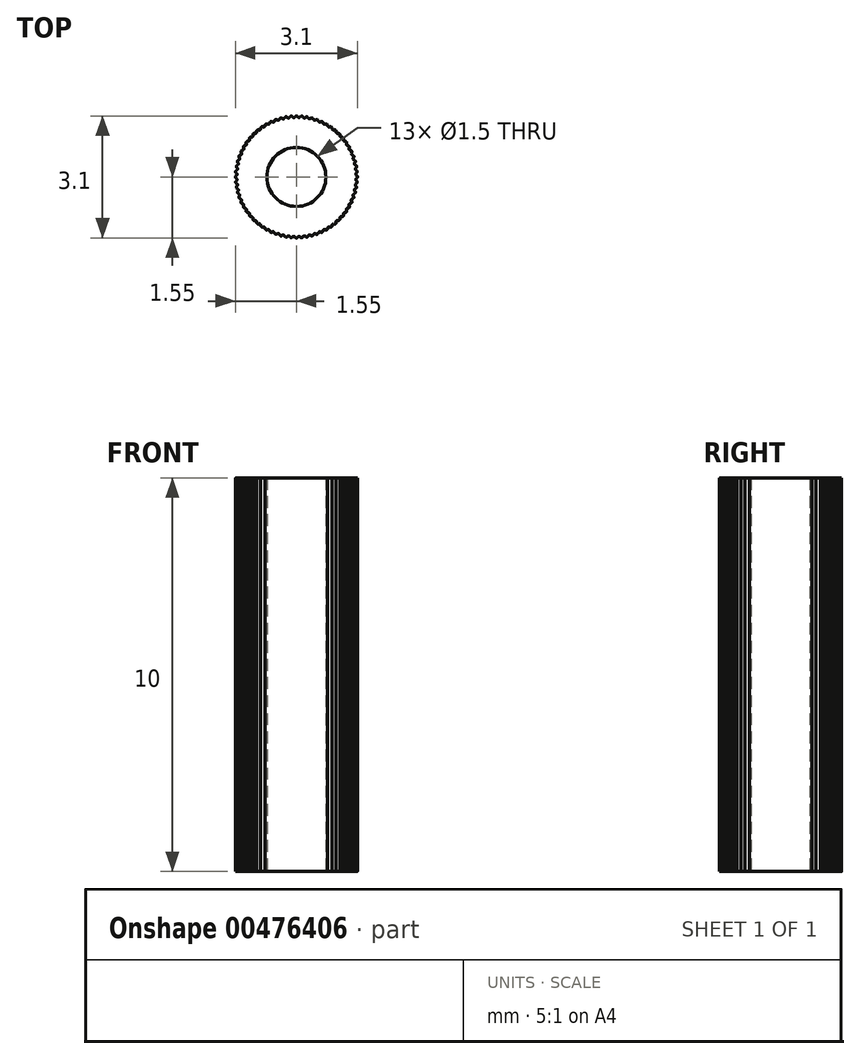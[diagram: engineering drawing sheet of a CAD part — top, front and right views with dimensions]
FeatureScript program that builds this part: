
annotation { "Feature Type Name" : "Feature", "Feature Type Description" : "" }
export const myFeature = defineFeature(function(context is Context, id is Id, definition is map)
    precondition{}
    {
        {
            var Q0;
            Q0=qCreatedBy(makeId("Top.planeOp"),FACE);
            var sketch = newSketch(context, id + "F0", { "sketchPlane" : qUnion([Q0])});
            skCircle(sketch, "E0", {"center": v(0, 0) * mm, "radius": 0.75 * mm});
            skCircle(sketch, "E1", {"center": v(0, 0) * mm, "radius": 1.55 * mm, "construction": true});
            skLineSegment(sketch, "E2", {"start": v(0, 0) * mm, "end": v(0, 1.55) * mm, "construction": true});
            skLineSegment(sketch, "E3", {"start": v(0, 0) * mm, "end": v(0.14, 1.54) * mm, "construction": true});
            skArc(sketch, "E4", {"start": v(0.03, 1.53) * mm, "mid": v(0.02, 1.54) * mm, "end": v(0, 1.55) * mm});
            skArc(sketch, "E5", {"start": v(0.03, 1.53) * mm, "mid": v(0.07, 1.51) * mm, "end": v(0.1, 1.53) * mm});
            skArc(sketch, "E6", {"start": v(0.14, 1.54) * mm, "mid": v(0.12, 1.54) * mm, "end": v(0.1, 1.53) * mm});
            skCircle(sketch, "E7", {"center": v(0, 0) * mm, "radius": 1.51 * mm, "construction": true});
            skArc(sketch, "E8.1.0", {"start": v(-0.1, 1.53) * mm, "mid": v(-0.12, 1.54) * mm, "end": v(-0.14, 1.54) * mm});
            skArc(sketch, "E8.1.1", {"start": v(-0.1, 1.53) * mm, "mid": v(-0.07, 1.51) * mm, "end": v(-0.03, 1.53) * mm});
            skArc(sketch, "E8.1.2", {"start": v(0, 1.55) * mm, "mid": v(-0.02, 1.54) * mm, "end": v(-0.03, 1.53) * mm});
            skArc(sketch, "E8.2.0", {"start": v(-0.23, 1.51) * mm, "mid": v(-0.25, 1.52) * mm, "end": v(-0.27, 1.53) * mm});
            skArc(sketch, "E8.2.1", {"start": v(-0.23, 1.51) * mm, "mid": v(-0.2, 1.5) * mm, "end": v(-0.17, 1.52) * mm});
            skArc(sketch, "E8.2.2", {"start": v(-0.14, 1.54) * mm, "mid": v(-0.15, 1.54) * mm, "end": v(-0.17, 1.52) * mm});
            skArc(sketch, "E8.3.0", {"start": v(-0.36, 1.49) * mm, "mid": v(-0.38, 1.5) * mm, "end": v(-0.4, 1.5) * mm});
            skArc(sketch, "E8.3.1", {"start": v(-0.36, 1.49) * mm, "mid": v(-0.33, 1.48) * mm, "end": v(-0.3, 1.5) * mm});
            skArc(sketch, "E8.3.2", {"start": v(-0.27, 1.53) * mm, "mid": v(-0.29, 1.52) * mm, "end": v(-0.3, 1.5) * mm});
            skArc(sketch, "E8.4.0", {"start": v(-0.5, 1.45) * mm, "mid": v(-0.5, 1.46) * mm, "end": v(-0.53, 1.46) * mm});
            skArc(sketch, "E8.4.1", {"start": v(-0.5, 1.45) * mm, "mid": v(-0.45, 1.44) * mm, "end": v(-0.43, 1.47) * mm});
            skArc(sketch, "E8.4.2", {"start": v(-0.4, 1.5) * mm, "mid": v(-0.42, 1.49) * mm, "end": v(-0.43, 1.47) * mm});
            skArc(sketch, "E8.5.0", {"start": v(-0.62, 1.4) * mm, "mid": v(-0.63, 1.4) * mm, "end": v(-0.66, 1.4) * mm});
            skArc(sketch, "E8.5.1", {"start": v(-0.62, 1.4) * mm, "mid": v(-0.58, 1.4) * mm, "end": v(-0.56, 1.43) * mm});
            skArc(sketch, "E8.5.2", {"start": v(-0.53, 1.46) * mm, "mid": v(-0.55, 1.44) * mm, "end": v(-0.56, 1.43) * mm});
            skArc(sketch, "E8.6.0", {"start": v(-0.74, 1.34) * mm, "mid": v(-0.76, 1.35) * mm, "end": v(-0.78, 1.34) * mm});
            skArc(sketch, "E8.6.1", {"start": v(-0.74, 1.34) * mm, "mid": v(-0.7, 1.34) * mm, "end": v(-0.68, 1.37) * mm});
            skArc(sketch, "E8.6.2", {"start": v(-0.66, 1.4) * mm, "mid": v(-0.67, 1.4) * mm, "end": v(-0.68, 1.37) * mm});
            skArc(sketch, "E8.7.0", {"start": v(-0.85, 1.27) * mm, "mid": v(-0.87, 1.28) * mm, "end": v(-0.89, 1.27) * mm});
            skArc(sketch, "E8.7.1", {"start": v(-0.85, 1.27) * mm, "mid": v(-0.81, 1.27) * mm, "end": v(-0.8, 1.3) * mm});
            skArc(sketch, "E8.7.2", {"start": v(-0.78, 1.34) * mm, "mid": v(-0.79, 1.33) * mm, "end": v(-0.8, 1.3) * mm});
            skArc(sketch, "E8.8.0", {"start": v(-0.96, 1.2) * mm, "mid": v(-0.98, 1.2) * mm, "end": v(-1, 1.19) * mm});
            skArc(sketch, "E8.8.1", {"start": v(-0.96, 1.2) * mm, "mid": v(-0.92, 1.2) * mm, "end": v(-0.9, 1.23) * mm});
            skArc(sketch, "E8.8.2", {"start": v(-0.89, 1.27) * mm, "mid": v(-0.9, 1.25) * mm, "end": v(-0.9, 1.23) * mm});
            skArc(sketch, "E8.9.0", {"start": v(-1.06, 1.1) * mm, "mid": v(-1.08, 1.1) * mm, "end": v(-1.1, 1.1) * mm});
            skArc(sketch, "E8.9.1", {"start": v(-1.06, 1.1) * mm, "mid": v(-1.02, 1.11) * mm, "end": v(-1, 1.15) * mm});
            skArc(sketch, "E8.9.2", {"start": v(-1, 1.19) * mm, "mid": v(-1, 1.17) * mm, "end": v(-1, 1.15) * mm});
            skArc(sketch, "E8.10.0", {"start": v(-1.15, 1) * mm, "mid": v(-1.17, 1) * mm, "end": v(-1.19, 1) * mm});
            skArc(sketch, "E8.10.1", {"start": v(-1.15, 1) * mm, "mid": v(-1.11, 1.02) * mm, "end": v(-1.1, 1.06) * mm});
            skArc(sketch, "E8.10.2", {"start": v(-1.1, 1.1) * mm, "mid": v(-1.1, 1.08) * mm, "end": v(-1.1, 1.06) * mm});
            skArc(sketch, "E8.11.0", {"start": v(-1.23, 0.9) * mm, "mid": v(-1.25, 0.9) * mm, "end": v(-1.27, 0.89) * mm});
            skArc(sketch, "E8.11.1", {"start": v(-1.23, 0.9) * mm, "mid": v(-1.2, 0.92) * mm, "end": v(-1.2, 0.96) * mm});
            skArc(sketch, "E8.11.2", {"start": v(-1.19, 1) * mm, "mid": v(-1.2, 0.98) * mm, "end": v(-1.2, 0.96) * mm});
            skArc(sketch, "E8.12.0", {"start": v(-1.3, 0.8) * mm, "mid": v(-1.33, 0.79) * mm, "end": v(-1.34, 0.78) * mm});
            skArc(sketch, "E8.12.1", {"start": v(-1.3, 0.8) * mm, "mid": v(-1.27, 0.81) * mm, "end": v(-1.27, 0.85) * mm});
            skArc(sketch, "E8.12.2", {"start": v(-1.27, 0.89) * mm, "mid": v(-1.28, 0.87) * mm, "end": v(-1.27, 0.85) * mm});
            skArc(sketch, "E8.13.0", {"start": v(-1.37, 0.68) * mm, "mid": v(-1.4, 0.67) * mm, "end": v(-1.4, 0.66) * mm});
            skArc(sketch, "E8.13.1", {"start": v(-1.37, 0.68) * mm, "mid": v(-1.34, 0.7) * mm, "end": v(-1.34, 0.74) * mm});
            skArc(sketch, "E8.13.2", {"start": v(-1.34, 0.77) * mm, "mid": v(-1.35, 0.76) * mm, "end": v(-1.34, 0.74) * mm});
            skArc(sketch, "E8.14.0", {"start": v(-1.43, 0.56) * mm, "mid": v(-1.44, 0.55) * mm, "end": v(-1.46, 0.53) * mm});
            skArc(sketch, "E8.14.1", {"start": v(-1.43, 0.56) * mm, "mid": v(-1.4, 0.58) * mm, "end": v(-1.4, 0.62) * mm});
            skArc(sketch, "E8.14.2", {"start": v(-1.4, 0.66) * mm, "mid": v(-1.4, 0.63) * mm, "end": v(-1.4, 0.62) * mm});
            skArc(sketch, "E8.15.0", {"start": v(-1.47, 0.43) * mm, "mid": v(-1.49, 0.42) * mm, "end": v(-1.5, 0.4) * mm});
            skArc(sketch, "E8.15.1", {"start": v(-1.47, 0.43) * mm, "mid": v(-1.44, 0.45) * mm, "end": v(-1.45, 0.5) * mm});
            skArc(sketch, "E8.15.2", {"start": v(-1.46, 0.53) * mm, "mid": v(-1.46, 0.5) * mm, "end": v(-1.45, 0.5) * mm});
            skArc(sketch, "E8.16.0", {"start": v(-1.5, 0.3) * mm, "mid": v(-1.52, 0.29) * mm, "end": v(-1.53, 0.27) * mm});
            skArc(sketch, "E8.16.1", {"start": v(-1.5, 0.3) * mm, "mid": v(-1.48, 0.33) * mm, "end": v(-1.49, 0.36) * mm});
            skArc(sketch, "E8.16.2", {"start": v(-1.5, 0.4) * mm, "mid": v(-1.5, 0.38) * mm, "end": v(-1.49, 0.36) * mm});
            skArc(sketch, "E8.17.0", {"start": v(-1.52, 0.17) * mm, "mid": v(-1.54, 0.15) * mm, "end": v(-1.54, 0.14) * mm});
            skArc(sketch, "E8.17.1", {"start": v(-1.52, 0.17) * mm, "mid": v(-1.5, 0.2) * mm, "end": v(-1.51, 0.23) * mm});
            skArc(sketch, "E8.17.2", {"start": v(-1.53, 0.27) * mm, "mid": v(-1.52, 0.25) * mm, "end": v(-1.51, 0.23) * mm});
            skArc(sketch, "E8.18.0", {"start": v(-1.53, 0.03) * mm, "mid": v(-1.54, 0.02) * mm, "end": v(-1.55, 0) * mm});
            skArc(sketch, "E8.18.1", {"start": v(-1.53, 0.03) * mm, "mid": v(-1.51, 0.07) * mm, "end": v(-1.53, 0.1) * mm});
            skArc(sketch, "E8.18.2", {"start": v(-1.54, 0.14) * mm, "mid": v(-1.54, 0.12) * mm, "end": v(-1.53, 0.1) * mm});
            skArc(sketch, "E8.19.0", {"start": v(-1.53, -0.1) * mm, "mid": v(-1.54, -0.12) * mm, "end": v(-1.54, -0.14) * mm});
            skArc(sketch, "E8.19.1", {"start": v(-1.53, -0.1) * mm, "mid": v(-1.51, -0.07) * mm, "end": v(-1.53, -0.03) * mm});
            skArc(sketch, "E8.19.2", {"start": v(-1.55, 0) * mm, "mid": v(-1.54, -0.02) * mm, "end": v(-1.53, -0.03) * mm});
            skArc(sketch, "E8.20.0", {"start": v(-1.51, -0.23) * mm, "mid": v(-1.52, -0.25) * mm, "end": v(-1.53, -0.27) * mm});
            skArc(sketch, "E8.20.1", {"start": v(-1.51, -0.23) * mm, "mid": v(-1.5, -0.2) * mm, "end": v(-1.52, -0.17) * mm});
            skArc(sketch, "E8.20.2", {"start": v(-1.54, -0.14) * mm, "mid": v(-1.54, -0.15) * mm, "end": v(-1.52, -0.17) * mm});
            skArc(sketch, "E8.21.0", {"start": v(-1.49, -0.36) * mm, "mid": v(-1.5, -0.38) * mm, "end": v(-1.5, -0.4) * mm});
            skArc(sketch, "E8.21.1", {"start": v(-1.49, -0.36) * mm, "mid": v(-1.48, -0.33) * mm, "end": v(-1.5, -0.3) * mm});
            skArc(sketch, "E8.21.2", {"start": v(-1.53, -0.27) * mm, "mid": v(-1.52, -0.29) * mm, "end": v(-1.5, -0.3) * mm});
            skArc(sketch, "E8.22.0", {"start": v(-1.45, -0.5) * mm, "mid": v(-1.46, -0.5) * mm, "end": v(-1.46, -0.53) * mm});
            skArc(sketch, "E8.22.1", {"start": v(-1.45, -0.5) * mm, "mid": v(-1.44, -0.45) * mm, "end": v(-1.47, -0.43) * mm});
            skArc(sketch, "E8.22.2", {"start": v(-1.5, -0.4) * mm, "mid": v(-1.49, -0.42) * mm, "end": v(-1.47, -0.43) * mm});
            skArc(sketch, "E8.23.0", {"start": v(-1.4, -0.62) * mm, "mid": v(-1.4, -0.63) * mm, "end": v(-1.4, -0.66) * mm});
            skArc(sketch, "E8.23.1", {"start": v(-1.4, -0.62) * mm, "mid": v(-1.4, -0.58) * mm, "end": v(-1.43, -0.56) * mm});
            skArc(sketch, "E8.23.2", {"start": v(-1.46, -0.53) * mm, "mid": v(-1.44, -0.55) * mm, "end": v(-1.43, -0.56) * mm});
            skArc(sketch, "E8.24.0", {"start": v(-1.34, -0.74) * mm, "mid": v(-1.35, -0.76) * mm, "end": v(-1.34, -0.77) * mm});
            skArc(sketch, "E8.24.1", {"start": v(-1.34, -0.74) * mm, "mid": v(-1.34, -0.7) * mm, "end": v(-1.37, -0.68) * mm});
            skArc(sketch, "E8.24.2", {"start": v(-1.4, -0.66) * mm, "mid": v(-1.4, -0.67) * mm, "end": v(-1.37, -0.68) * mm});
            skArc(sketch, "E8.25.0", {"start": v(-1.27, -0.85) * mm, "mid": v(-1.28, -0.87) * mm, "end": v(-1.27, -0.89) * mm});
            skArc(sketch, "E8.25.1", {"start": v(-1.27, -0.85) * mm, "mid": v(-1.27, -0.81) * mm, "end": v(-1.3, -0.8) * mm});
            skArc(sketch, "E8.25.2", {"start": v(-1.34, -0.78) * mm, "mid": v(-1.33, -0.79) * mm, "end": v(-1.3, -0.8) * mm});
            skArc(sketch, "E8.26.0", {"start": v(-1.2, -0.96) * mm, "mid": v(-1.2, -0.98) * mm, "end": v(-1.19, -1) * mm});
            skArc(sketch, "E8.26.1", {"start": v(-1.2, -0.96) * mm, "mid": v(-1.2, -0.92) * mm, "end": v(-1.23, -0.9) * mm});
            skArc(sketch, "E8.26.2", {"start": v(-1.27, -0.89) * mm, "mid": v(-1.25, -0.9) * mm, "end": v(-1.23, -0.9) * mm});
            skArc(sketch, "E8.27.0", {"start": v(-1.1, -1.06) * mm, "mid": v(-1.1, -1.08) * mm, "end": v(-1.1, -1.1) * mm});
            skArc(sketch, "E8.27.1", {"start": v(-1.1, -1.06) * mm, "mid": v(-1.11, -1.02) * mm, "end": v(-1.15, -1) * mm});
            skArc(sketch, "E8.27.2", {"start": v(-1.19, -1) * mm, "mid": v(-1.17, -1) * mm, "end": v(-1.15, -1) * mm});
            skArc(sketch, "E8.28.0", {"start": v(-1, -1.15) * mm, "mid": v(-1, -1.17) * mm, "end": v(-1, -1.19) * mm});
            skArc(sketch, "E8.28.1", {"start": v(-1, -1.15) * mm, "mid": v(-1.02, -1.11) * mm, "end": v(-1.06, -1.1) * mm});
            skArc(sketch, "E8.28.2", {"start": v(-1.1, -1.1) * mm, "mid": v(-1.08, -1.1) * mm, "end": v(-1.06, -1.1) * mm});
            skArc(sketch, "E8.29.0", {"start": v(-0.9, -1.23) * mm, "mid": v(-0.9, -1.25) * mm, "end": v(-0.89, -1.27) * mm});
            skArc(sketch, "E8.29.1", {"start": v(-0.9, -1.23) * mm, "mid": v(-0.92, -1.2) * mm, "end": v(-0.96, -1.2) * mm});
            skArc(sketch, "E8.29.2", {"start": v(-1, -1.19) * mm, "mid": v(-0.98, -1.2) * mm, "end": v(-0.96, -1.2) * mm});
            skArc(sketch, "E8.30.0", {"start": v(-0.8, -1.3) * mm, "mid": v(-0.79, -1.33) * mm, "end": v(-0.77, -1.34) * mm});
            skArc(sketch, "E8.30.1", {"start": v(-0.8, -1.3) * mm, "mid": v(-0.81, -1.27) * mm, "end": v(-0.85, -1.27) * mm});
            skArc(sketch, "E8.30.2", {"start": v(-0.89, -1.27) * mm, "mid": v(-0.87, -1.28) * mm, "end": v(-0.85, -1.27) * mm});
            skArc(sketch, "E8.31.0", {"start": v(-0.68, -1.37) * mm, "mid": v(-0.67, -1.4) * mm, "end": v(-0.66, -1.4) * mm});
            skArc(sketch, "E8.31.1", {"start": v(-0.68, -1.37) * mm, "mid": v(-0.7, -1.34) * mm, "end": v(-0.74, -1.34) * mm});
            skArc(sketch, "E8.31.2", {"start": v(-0.77, -1.34) * mm, "mid": v(-0.76, -1.35) * mm, "end": v(-0.74, -1.34) * mm});
            skArc(sketch, "E8.32.0", {"start": v(-0.56, -1.43) * mm, "mid": v(-0.55, -1.44) * mm, "end": v(-0.53, -1.46) * mm});
            skArc(sketch, "E8.32.1", {"start": v(-0.56, -1.43) * mm, "mid": v(-0.58, -1.4) * mm, "end": v(-0.62, -1.4) * mm});
            skArc(sketch, "E8.32.2", {"start": v(-0.66, -1.4) * mm, "mid": v(-0.63, -1.4) * mm, "end": v(-0.62, -1.4) * mm});
            skArc(sketch, "E8.33.0", {"start": v(-0.43, -1.47) * mm, "mid": v(-0.42, -1.49) * mm, "end": v(-0.4, -1.5) * mm});
            skArc(sketch, "E8.33.1", {"start": v(-0.43, -1.47) * mm, "mid": v(-0.45, -1.44) * mm, "end": v(-0.5, -1.45) * mm});
            skArc(sketch, "E8.33.2", {"start": v(-0.53, -1.46) * mm, "mid": v(-0.5, -1.46) * mm, "end": v(-0.5, -1.45) * mm});
            skArc(sketch, "E8.34.0", {"start": v(-0.3, -1.5) * mm, "mid": v(-0.29, -1.52) * mm, "end": v(-0.27, -1.53) * mm});
            skArc(sketch, "E8.34.1", {"start": v(-0.3, -1.5) * mm, "mid": v(-0.33, -1.48) * mm, "end": v(-0.36, -1.49) * mm});
            skArc(sketch, "E8.34.2", {"start": v(-0.4, -1.5) * mm, "mid": v(-0.38, -1.5) * mm, "end": v(-0.36, -1.49) * mm});
            skArc(sketch, "E8.35.0", {"start": v(-0.17, -1.52) * mm, "mid": v(-0.15, -1.54) * mm, "end": v(-0.14, -1.54) * mm});
            skArc(sketch, "E8.35.1", {"start": v(-0.17, -1.52) * mm, "mid": v(-0.2, -1.5) * mm, "end": v(-0.23, -1.51) * mm});
            skArc(sketch, "E8.35.2", {"start": v(-0.27, -1.53) * mm, "mid": v(-0.25, -1.52) * mm, "end": v(-0.23, -1.51) * mm});
            skArc(sketch, "E8.36.0", {"start": v(-0.03, -1.53) * mm, "mid": v(-0.02, -1.54) * mm, "end": v(0, -1.55) * mm});
            skArc(sketch, "E8.36.1", {"start": v(-0.03, -1.53) * mm, "mid": v(-0.07, -1.51) * mm, "end": v(-0.1, -1.53) * mm});
            skArc(sketch, "E8.36.2", {"start": v(-0.14, -1.54) * mm, "mid": v(-0.12, -1.54) * mm, "end": v(-0.1, -1.53) * mm});
            skArc(sketch, "E8.37.0", {"start": v(0.1, -1.53) * mm, "mid": v(0.12, -1.54) * mm, "end": v(0.14, -1.54) * mm});
            skArc(sketch, "E8.37.1", {"start": v(0.1, -1.53) * mm, "mid": v(0.07, -1.51) * mm, "end": v(0.03, -1.53) * mm});
            skArc(sketch, "E8.37.2", {"start": v(0, -1.55) * mm, "mid": v(0.02, -1.54) * mm, "end": v(0.03, -1.53) * mm});
            skArc(sketch, "E8.38.0", {"start": v(0.23, -1.51) * mm, "mid": v(0.25, -1.52) * mm, "end": v(0.27, -1.53) * mm});
            skArc(sketch, "E8.38.1", {"start": v(0.23, -1.51) * mm, "mid": v(0.2, -1.5) * mm, "end": v(0.17, -1.52) * mm});
            skArc(sketch, "E8.38.2", {"start": v(0.14, -1.54) * mm, "mid": v(0.15, -1.54) * mm, "end": v(0.17, -1.52) * mm});
            skArc(sketch, "E8.39.0", {"start": v(0.36, -1.49) * mm, "mid": v(0.38, -1.5) * mm, "end": v(0.4, -1.5) * mm});
            skArc(sketch, "E8.39.1", {"start": v(0.36, -1.49) * mm, "mid": v(0.33, -1.48) * mm, "end": v(0.3, -1.5) * mm});
            skArc(sketch, "E8.39.2", {"start": v(0.27, -1.53) * mm, "mid": v(0.29, -1.52) * mm, "end": v(0.3, -1.5) * mm});
            skArc(sketch, "E8.40.0", {"start": v(0.5, -1.45) * mm, "mid": v(0.5, -1.46) * mm, "end": v(0.53, -1.46) * mm});
            skArc(sketch, "E8.40.1", {"start": v(0.5, -1.45) * mm, "mid": v(0.45, -1.44) * mm, "end": v(0.43, -1.47) * mm});
            skArc(sketch, "E8.40.2", {"start": v(0.4, -1.5) * mm, "mid": v(0.42, -1.49) * mm, "end": v(0.43, -1.47) * mm});
            skArc(sketch, "E8.41.0", {"start": v(0.62, -1.4) * mm, "mid": v(0.63, -1.4) * mm, "end": v(0.66, -1.4) * mm});
            skArc(sketch, "E8.41.1", {"start": v(0.62, -1.4) * mm, "mid": v(0.58, -1.4) * mm, "end": v(0.56, -1.43) * mm});
            skArc(sketch, "E8.41.2", {"start": v(0.53, -1.46) * mm, "mid": v(0.55, -1.44) * mm, "end": v(0.56, -1.43) * mm});
            skArc(sketch, "E8.42.0", {"start": v(0.74, -1.34) * mm, "mid": v(0.76, -1.35) * mm, "end": v(0.77, -1.34) * mm});
            skArc(sketch, "E8.42.1", {"start": v(0.74, -1.34) * mm, "mid": v(0.7, -1.34) * mm, "end": v(0.68, -1.37) * mm});
            skArc(sketch, "E8.42.2", {"start": v(0.66, -1.4) * mm, "mid": v(0.67, -1.4) * mm, "end": v(0.68, -1.37) * mm});
            skArc(sketch, "E8.43.0", {"start": v(0.85, -1.27) * mm, "mid": v(0.87, -1.28) * mm, "end": v(0.89, -1.27) * mm});
            skArc(sketch, "E8.43.1", {"start": v(0.85, -1.27) * mm, "mid": v(0.81, -1.27) * mm, "end": v(0.8, -1.3) * mm});
            skArc(sketch, "E8.43.2", {"start": v(0.78, -1.34) * mm, "mid": v(0.79, -1.33) * mm, "end": v(0.8, -1.3) * mm});
            skArc(sketch, "E8.44.0", {"start": v(0.96, -1.2) * mm, "mid": v(0.98, -1.2) * mm, "end": v(1, -1.19) * mm});
            skArc(sketch, "E8.44.1", {"start": v(0.96, -1.2) * mm, "mid": v(0.92, -1.2) * mm, "end": v(0.9, -1.23) * mm});
            skArc(sketch, "E8.44.2", {"start": v(0.89, -1.27) * mm, "mid": v(0.9, -1.25) * mm, "end": v(0.9, -1.23) * mm});
            skArc(sketch, "E8.45.0", {"start": v(1.06, -1.1) * mm, "mid": v(1.08, -1.1) * mm, "end": v(1.1, -1.1) * mm});
            skArc(sketch, "E8.45.1", {"start": v(1.06, -1.1) * mm, "mid": v(1.02, -1.11) * mm, "end": v(1, -1.15) * mm});
            skArc(sketch, "E8.45.2", {"start": v(1, -1.19) * mm, "mid": v(1, -1.17) * mm, "end": v(1, -1.15) * mm});
            skArc(sketch, "E8.46.0", {"start": v(1.15, -1) * mm, "mid": v(1.17, -1) * mm, "end": v(1.19, -1) * mm});
            skArc(sketch, "E8.46.1", {"start": v(1.15, -1) * mm, "mid": v(1.11, -1.02) * mm, "end": v(1.1, -1.06) * mm});
            skArc(sketch, "E8.46.2", {"start": v(1.1, -1.1) * mm, "mid": v(1.1, -1.08) * mm, "end": v(1.1, -1.06) * mm});
            skArc(sketch, "E8.47.0", {"start": v(1.23, -0.9) * mm, "mid": v(1.25, -0.9) * mm, "end": v(1.27, -0.89) * mm});
            skArc(sketch, "E8.47.1", {"start": v(1.23, -0.9) * mm, "mid": v(1.2, -0.92) * mm, "end": v(1.2, -0.96) * mm});
            skArc(sketch, "E8.47.2", {"start": v(1.19, -1) * mm, "mid": v(1.2, -0.98) * mm, "end": v(1.2, -0.96) * mm});
            skArc(sketch, "E8.48.0", {"start": v(1.3, -0.8) * mm, "mid": v(1.33, -0.79) * mm, "end": v(1.34, -0.78) * mm});
            skArc(sketch, "E8.48.1", {"start": v(1.3, -0.8) * mm, "mid": v(1.27, -0.81) * mm, "end": v(1.27, -0.85) * mm});
            skArc(sketch, "E8.48.2", {"start": v(1.27, -0.89) * mm, "mid": v(1.28, -0.87) * mm, "end": v(1.27, -0.85) * mm});
            skArc(sketch, "E8.49.0", {"start": v(1.37, -0.68) * mm, "mid": v(1.4, -0.67) * mm, "end": v(1.4, -0.66) * mm});
            skArc(sketch, "E8.49.1", {"start": v(1.37, -0.68) * mm, "mid": v(1.34, -0.7) * mm, "end": v(1.34, -0.74) * mm});
            skArc(sketch, "E8.49.2", {"start": v(1.34, -0.78) * mm, "mid": v(1.35, -0.76) * mm, "end": v(1.34, -0.74) * mm});
            skArc(sketch, "E8.50.0", {"start": v(1.43, -0.56) * mm, "mid": v(1.44, -0.55) * mm, "end": v(1.46, -0.53) * mm});
            skArc(sketch, "E8.50.1", {"start": v(1.43, -0.56) * mm, "mid": v(1.4, -0.58) * mm, "end": v(1.4, -0.62) * mm});
            skArc(sketch, "E8.50.2", {"start": v(1.4, -0.66) * mm, "mid": v(1.4, -0.63) * mm, "end": v(1.4, -0.62) * mm});
            skArc(sketch, "E8.51.0", {"start": v(1.47, -0.43) * mm, "mid": v(1.49, -0.42) * mm, "end": v(1.5, -0.4) * mm});
            skArc(sketch, "E8.51.1", {"start": v(1.47, -0.43) * mm, "mid": v(1.44, -0.45) * mm, "end": v(1.45, -0.5) * mm});
            skArc(sketch, "E8.51.2", {"start": v(1.46, -0.53) * mm, "mid": v(1.46, -0.5) * mm, "end": v(1.45, -0.5) * mm});
            skArc(sketch, "E8.52.0", {"start": v(1.5, -0.3) * mm, "mid": v(1.52, -0.29) * mm, "end": v(1.53, -0.27) * mm});
            skArc(sketch, "E8.52.1", {"start": v(1.5, -0.3) * mm, "mid": v(1.48, -0.33) * mm, "end": v(1.49, -0.36) * mm});
            skArc(sketch, "E8.52.2", {"start": v(1.5, -0.4) * mm, "mid": v(1.5, -0.38) * mm, "end": v(1.49, -0.36) * mm});
            skArc(sketch, "E8.53.0", {"start": v(1.52, -0.17) * mm, "mid": v(1.54, -0.15) * mm, "end": v(1.54, -0.14) * mm});
            skArc(sketch, "E8.53.1", {"start": v(1.52, -0.17) * mm, "mid": v(1.5, -0.2) * mm, "end": v(1.51, -0.23) * mm});
            skArc(sketch, "E8.53.2", {"start": v(1.53, -0.27) * mm, "mid": v(1.52, -0.25) * mm, "end": v(1.51, -0.23) * mm});
            skArc(sketch, "E8.54.0", {"start": v(1.53, -0.03) * mm, "mid": v(1.54, -0.02) * mm, "end": v(1.55, 0) * mm});
            skArc(sketch, "E8.54.1", {"start": v(1.53, -0.03) * mm, "mid": v(1.51, -0.07) * mm, "end": v(1.53, -0.1) * mm});
            skArc(sketch, "E8.54.2", {"start": v(1.54, -0.14) * mm, "mid": v(1.54, -0.12) * mm, "end": v(1.53, -0.1) * mm});
            skArc(sketch, "E8.55.0", {"start": v(1.53, 0.1) * mm, "mid": v(1.54, 0.12) * mm, "end": v(1.54, 0.14) * mm});
            skArc(sketch, "E8.55.1", {"start": v(1.53, 0.1) * mm, "mid": v(1.51, 0.07) * mm, "end": v(1.53, 0.03) * mm});
            skArc(sketch, "E8.55.2", {"start": v(1.55, 0) * mm, "mid": v(1.54, 0.02) * mm, "end": v(1.53, 0.03) * mm});
            skArc(sketch, "E8.56.0", {"start": v(1.51, 0.23) * mm, "mid": v(1.52, 0.25) * mm, "end": v(1.53, 0.27) * mm});
            skArc(sketch, "E8.56.1", {"start": v(1.51, 0.23) * mm, "mid": v(1.5, 0.2) * mm, "end": v(1.52, 0.17) * mm});
            skArc(sketch, "E8.56.2", {"start": v(1.54, 0.14) * mm, "mid": v(1.54, 0.15) * mm, "end": v(1.52, 0.17) * mm});
            skArc(sketch, "E8.57.0", {"start": v(1.49, 0.36) * mm, "mid": v(1.5, 0.38) * mm, "end": v(1.5, 0.4) * mm});
            skArc(sketch, "E8.57.1", {"start": v(1.49, 0.36) * mm, "mid": v(1.48, 0.33) * mm, "end": v(1.5, 0.3) * mm});
            skArc(sketch, "E8.57.2", {"start": v(1.53, 0.27) * mm, "mid": v(1.52, 0.29) * mm, "end": v(1.5, 0.3) * mm});
            skArc(sketch, "E8.58.0", {"start": v(1.45, 0.5) * mm, "mid": v(1.46, 0.5) * mm, "end": v(1.46, 0.53) * mm});
            skArc(sketch, "E8.58.1", {"start": v(1.45, 0.5) * mm, "mid": v(1.44, 0.45) * mm, "end": v(1.47, 0.43) * mm});
            skArc(sketch, "E8.58.2", {"start": v(1.5, 0.4) * mm, "mid": v(1.49, 0.42) * mm, "end": v(1.47, 0.43) * mm});
            skArc(sketch, "E8.59.0", {"start": v(1.4, 0.62) * mm, "mid": v(1.4, 0.63) * mm, "end": v(1.4, 0.66) * mm});
            skArc(sketch, "E8.59.1", {"start": v(1.4, 0.62) * mm, "mid": v(1.4, 0.58) * mm, "end": v(1.43, 0.56) * mm});
            skArc(sketch, "E8.59.2", {"start": v(1.46, 0.53) * mm, "mid": v(1.44, 0.55) * mm, "end": v(1.43, 0.56) * mm});
            skArc(sketch, "E8.60.0", {"start": v(1.34, 0.74) * mm, "mid": v(1.35, 0.76) * mm, "end": v(1.34, 0.78) * mm});
            skArc(sketch, "E8.60.1", {"start": v(1.34, 0.74) * mm, "mid": v(1.34, 0.7) * mm, "end": v(1.37, 0.68) * mm});
            skArc(sketch, "E8.60.2", {"start": v(1.4, 0.66) * mm, "mid": v(1.4, 0.67) * mm, "end": v(1.37, 0.68) * mm});
            skArc(sketch, "E8.61.0", {"start": v(1.27, 0.85) * mm, "mid": v(1.28, 0.87) * mm, "end": v(1.27, 0.89) * mm});
            skArc(sketch, "E8.61.1", {"start": v(1.27, 0.85) * mm, "mid": v(1.27, 0.81) * mm, "end": v(1.3, 0.8) * mm});
            skArc(sketch, "E8.61.2", {"start": v(1.34, 0.78) * mm, "mid": v(1.33, 0.79) * mm, "end": v(1.3, 0.8) * mm});
            skArc(sketch, "E8.62.0", {"start": v(1.2, 0.96) * mm, "mid": v(1.2, 0.98) * mm, "end": v(1.19, 1) * mm});
            skArc(sketch, "E8.62.1", {"start": v(1.2, 0.96) * mm, "mid": v(1.2, 0.92) * mm, "end": v(1.23, 0.9) * mm});
            skArc(sketch, "E8.62.2", {"start": v(1.27, 0.89) * mm, "mid": v(1.25, 0.9) * mm, "end": v(1.23, 0.9) * mm});
            skArc(sketch, "E8.63.0", {"start": v(1.1, 1.06) * mm, "mid": v(1.1, 1.08) * mm, "end": v(1.1, 1.1) * mm});
            skArc(sketch, "E8.63.1", {"start": v(1.1, 1.06) * mm, "mid": v(1.11, 1.02) * mm, "end": v(1.15, 1) * mm});
            skArc(sketch, "E8.63.2", {"start": v(1.19, 1) * mm, "mid": v(1.17, 1) * mm, "end": v(1.15, 1) * mm});
            skArc(sketch, "E8.64.0", {"start": v(1, 1.15) * mm, "mid": v(1, 1.17) * mm, "end": v(1, 1.19) * mm});
            skArc(sketch, "E8.64.1", {"start": v(1, 1.15) * mm, "mid": v(1.02, 1.11) * mm, "end": v(1.06, 1.1) * mm});
            skArc(sketch, "E8.64.2", {"start": v(1.1, 1.1) * mm, "mid": v(1.08, 1.1) * mm, "end": v(1.06, 1.1) * mm});
            skArc(sketch, "E8.65.0", {"start": v(0.9, 1.23) * mm, "mid": v(0.9, 1.25) * mm, "end": v(0.89, 1.27) * mm});
            skArc(sketch, "E8.65.1", {"start": v(0.9, 1.23) * mm, "mid": v(0.92, 1.2) * mm, "end": v(0.96, 1.2) * mm});
            skArc(sketch, "E8.65.2", {"start": v(1, 1.19) * mm, "mid": v(0.98, 1.2) * mm, "end": v(0.96, 1.2) * mm});
            skArc(sketch, "E8.66.0", {"start": v(0.8, 1.3) * mm, "mid": v(0.79, 1.33) * mm, "end": v(0.78, 1.34) * mm});
            skArc(sketch, "E8.66.1", {"start": v(0.8, 1.3) * mm, "mid": v(0.81, 1.27) * mm, "end": v(0.85, 1.27) * mm});
            skArc(sketch, "E8.66.2", {"start": v(0.89, 1.27) * mm, "mid": v(0.87, 1.28) * mm, "end": v(0.85, 1.27) * mm});
            skArc(sketch, "E8.67.0", {"start": v(0.68, 1.37) * mm, "mid": v(0.67, 1.4) * mm, "end": v(0.66, 1.4) * mm});
            skArc(sketch, "E8.67.1", {"start": v(0.68, 1.37) * mm, "mid": v(0.7, 1.34) * mm, "end": v(0.74, 1.34) * mm});
            skArc(sketch, "E8.67.2", {"start": v(0.78, 1.34) * mm, "mid": v(0.76, 1.35) * mm, "end": v(0.74, 1.34) * mm});
            skArc(sketch, "E8.68.0", {"start": v(0.56, 1.43) * mm, "mid": v(0.55, 1.44) * mm, "end": v(0.53, 1.46) * mm});
            skArc(sketch, "E8.68.1", {"start": v(0.56, 1.43) * mm, "mid": v(0.58, 1.4) * mm, "end": v(0.62, 1.4) * mm});
            skArc(sketch, "E8.68.2", {"start": v(0.66, 1.4) * mm, "mid": v(0.63, 1.4) * mm, "end": v(0.62, 1.4) * mm});
            skArc(sketch, "E8.69.0", {"start": v(0.43, 1.47) * mm, "mid": v(0.42, 1.49) * mm, "end": v(0.4, 1.5) * mm});
            skArc(sketch, "E8.69.1", {"start": v(0.43, 1.47) * mm, "mid": v(0.45, 1.44) * mm, "end": v(0.5, 1.45) * mm});
            skArc(sketch, "E8.69.2", {"start": v(0.53, 1.46) * mm, "mid": v(0.5, 1.46) * mm, "end": v(0.5, 1.45) * mm});
            skArc(sketch, "E8.70.0", {"start": v(0.3, 1.5) * mm, "mid": v(0.29, 1.52) * mm, "end": v(0.27, 1.53) * mm});
            skArc(sketch, "E8.70.1", {"start": v(0.3, 1.5) * mm, "mid": v(0.33, 1.48) * mm, "end": v(0.36, 1.49) * mm});
            skArc(sketch, "E8.70.2", {"start": v(0.4, 1.5) * mm, "mid": v(0.38, 1.5) * mm, "end": v(0.36, 1.49) * mm});
            skArc(sketch, "E8.71.0", {"start": v(0.17, 1.52) * mm, "mid": v(0.15, 1.54) * mm, "end": v(0.14, 1.54) * mm});
            skArc(sketch, "E8.71.1", {"start": v(0.17, 1.52) * mm, "mid": v(0.2, 1.5) * mm, "end": v(0.23, 1.51) * mm});
            skArc(sketch, "E8.71.2", {"start": v(0.27, 1.53) * mm, "mid": v(0.25, 1.52) * mm, "end": v(0.23, 1.51) * mm});
            skSolve(sketch);
        }
        {
            var Q0;
            Q0=qSketchRegion(id+"F0",true);
            extrude(context, id + "F1", {"entities" : qUnion([Q0]), "depth" : 10 * mm});
        }
    });
